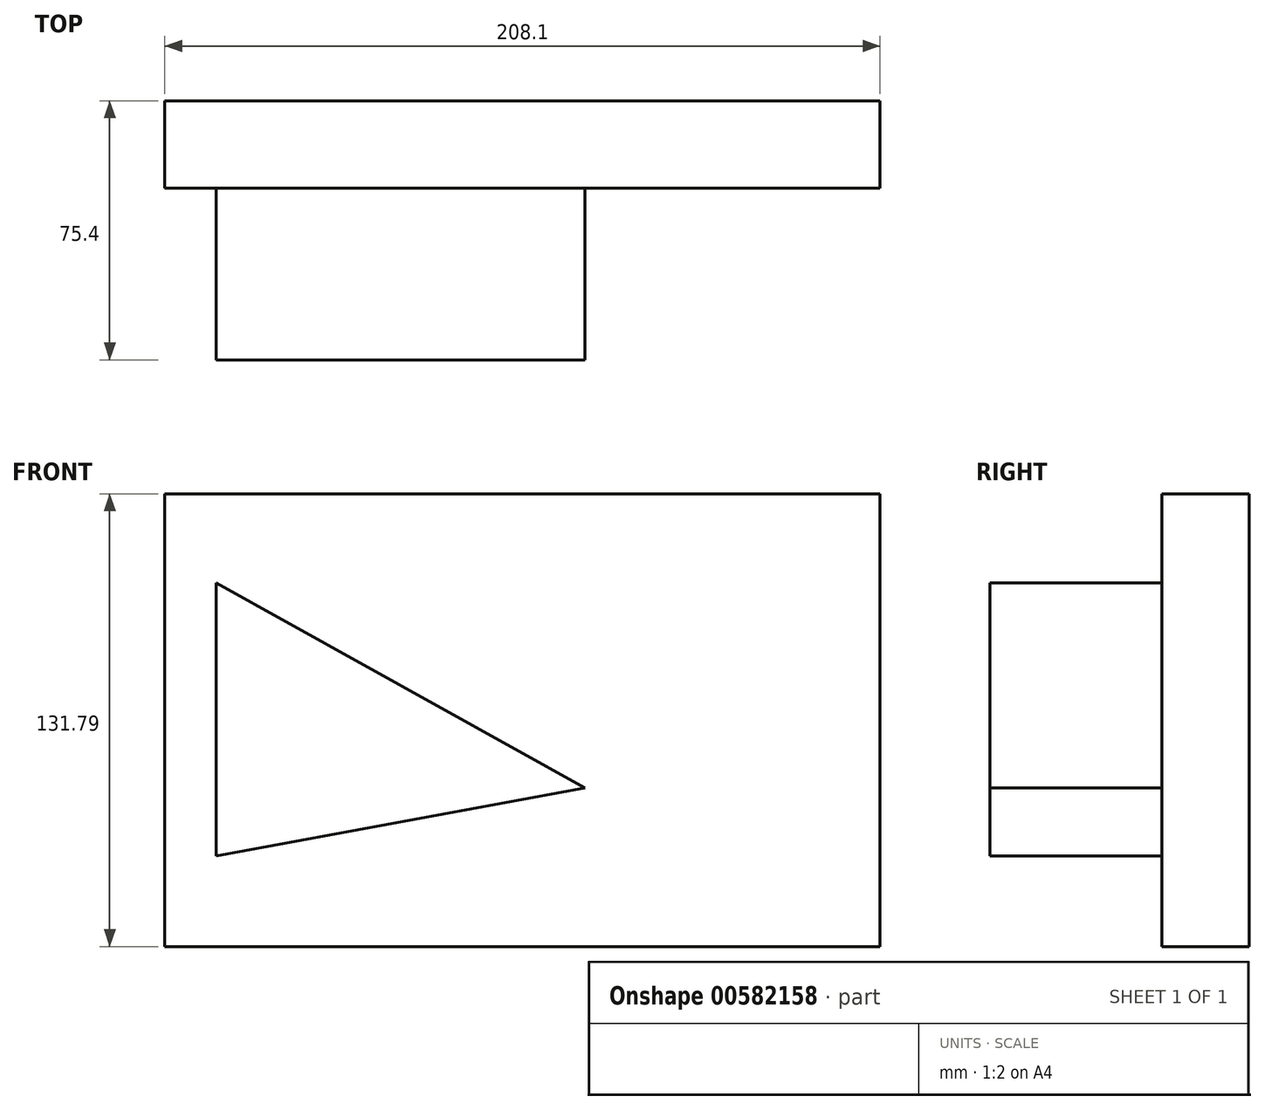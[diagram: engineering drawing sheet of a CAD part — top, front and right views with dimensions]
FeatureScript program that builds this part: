
annotation { "Feature Type Name" : "Feature", "Feature Type Description" : "" }
export const myFeature = defineFeature(function(context is Context, id is Id, definition is map)
    precondition{}
    {
        {
            var Q0;
            Q0=qCreatedBy(makeId("Front.planeOp"),FACE);
            var sketch = newSketch(context, id + "F0", { "sketchPlane" : qUnion([Q0])});
            skLineSegment(sketch, "E0.bottom", {"start": v(-122.24, -62) * mm, "end": v(85.86, -62) * mm});
            skLineSegment(sketch, "E0.top", {"start": v(-122.24, 69.8) * mm, "end": v(85.86, 69.8) * mm});
            skLineSegment(sketch, "E0.left", {"start": v(-122.24, -62) * mm, "end": v(-122.24, 69.8) * mm});
            skLineSegment(sketch, "E0.right", {"start": v(85.86, -62) * mm, "end": v(85.86, 69.8) * mm});
            skSolve(sketch);
        }
        {
            var Q0;
            Q0 = qSketchRegion(id + "F0", true);
            extrude(context, id + "F1", {"entities" : qUnion([Q0]), "depth" : 25.4 * mm, "offsetDistance" : 25.4 * mm});
        }
        {
            var Q0;
            Q0=makeQuery(id+"F1.opExtrude","CAP_FACE",FACE,{"disambiguationData":[OSD([sQuery(id+"F0.wireOp",EDGE,"E0.bottom"),sQuery(id+"F0.wireOp",EDGE,"E0.top"),sQuery(id+"F0.wireOp",EDGE,"E0.left"),sQuery(id+"F0.wireOp",EDGE,"E0.right")])],"isStart":false});
            var sketch = newSketch(context, id + "F2", { "sketchPlane" : qUnion([Q0])});
            skLineSegment(sketch, "E1", {"start": v(65.44, 50.59) * mm, "end": v(10.28, -48.08) * mm});
            skSolve(sketch);
        }
        {
            var Q0;
            Q0=makeQuery(id+"F2.imprint","IMPRINT",FACE,{"disambiguationData":[TD([[makeQuery(id+"F2.imprint","IMPRINT",EDGE,{"derivedFrom":makeQuery(id+"F1.opExtrude","CAP_EDGE",EDGE,{"disambiguationData":[OSD([sQuery(id+"F0.wireOp",EDGE,"E0.bottom")])],"isStart":false})}),1.0]])]});
            var sketch = newSketch(context, id + "F3", { "sketchPlane" : qUnion([Q0])});
            skLineSegment(sketch, "E2", {"start": v(0, -15.75) * mm, "end": v(-107.33, -35.65) * mm});
            skLineSegment(sketch, "E3", {"start": v(-107.33, -35.65) * mm, "end": v(-107.33, 43.82) * mm});
            skLineSegment(sketch, "E4", {"start": v(-107.33, 43.82) * mm, "end": v(0, -15.75) * mm});
            skSolve(sketch);
        }
        {
            var Q0;
            Q0 = qSketchRegion(id + "F3", true);
            extrude(context, id + "F4", {"entities" : qUnion([Q0]), "operationType" : NewBodyOperationType.ADD, "depth" : 50 * mm, "offsetDistance" : 25.4 * mm});
        }
    });
